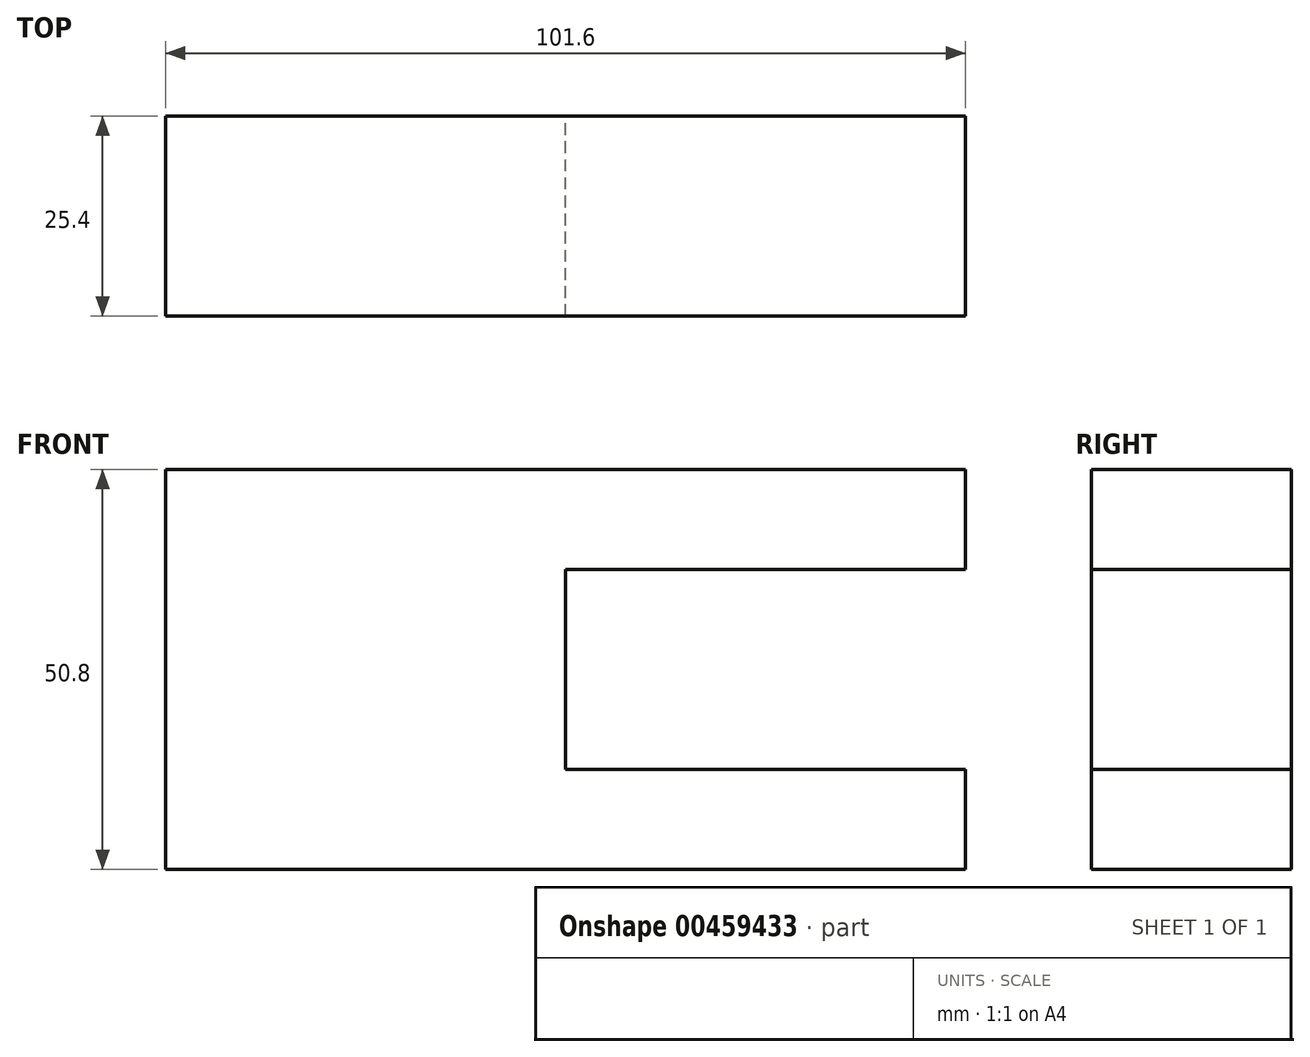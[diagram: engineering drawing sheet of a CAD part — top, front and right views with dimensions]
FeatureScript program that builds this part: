
annotation { "Feature Type Name" : "Feature", "Feature Type Description" : "" }
export const myFeature = defineFeature(function(context is Context, id is Id, definition is map)
    precondition{}
    {
        {
            var Q0;
            Q0=qCreatedBy(makeId("Front.planeOp"),FACE);
            var sketch = newSketch(context, id + "F0", { "sketchPlane" : qUnion([Q0])});
            skLineSegment(sketch, "E0.bottom", {"start": v(-50.8, 25.4) * mm, "end": v(50.8, 25.4) * mm});
            skLineSegment(sketch, "E0.top", {"start": v(-50.8, -25.4) * mm, "end": v(50.8, -25.4) * mm});
            skLineSegment(sketch, "E0.left", {"start": v(-50.8, 25.4) * mm, "end": v(-50.8, -25.4) * mm});
            skLineSegment(sketch, "E0.right", {"start": v(50.8, 25.4) * mm, "end": v(50.8, -25.4) * mm});
            skPoint(sketch, "E0.middle", {"position": v(0, 0) * mm});
            skSolve(sketch);
        }
        {
            var Q0;
            Q0=makeQuery(id+"F0.imprint","IMPRINT",FACE,{"disambiguationData":[TD([[makeQuery(id+"F0.imprint","IMPRINT",EDGE,{"derivedFrom":sQuery(id+"F0.wireOp",EDGE,"E0.bottom")}),-1.0]])]});
            extrude(context, id + "F1", {"entities" : qUnion([Q0]), "depth" : 25.4 * mm});
        }
        {
            var Q0;
            Q0=qCreatedBy(makeId("Front.planeOp"),FACE);
            var sketch = newSketch(context, id + "F2", { "sketchPlane" : qUnion([Q0])});
            skLineSegment(sketch, "E1.bottom", {"start": v(50.8, -12.7) * mm, "end": v(0, -12.7) * mm});
            skLineSegment(sketch, "E1.top", {"start": v(50.8, 12.7) * mm, "end": v(0, 12.7) * mm});
            skLineSegment(sketch, "E1.left", {"start": v(50.8, -12.7) * mm, "end": v(50.8, 12.7) * mm});
            skLineSegment(sketch, "E1.right", {"start": v(0, -12.7) * mm, "end": v(0, 12.7) * mm});
            skSolve(sketch);
        }
        {
            var Q0;
            Q0 = qSketchRegion(id + "F2", true);
            extrude(context, id + "F3", {"entities" : qUnion([Q0]), "operationType" : NewBodyOperationType.REMOVE, "endBound" : BoundingType.THROUGH_ALL, "oppositeDirection" : true, "depth" : 25.4 * mm});
        }
        {
            var Q0;
            Q0 = qSketchRegion(id + "F2", true);
            extrude(context, id + "F4", {"entities" : qUnion([Q0]), "operationType" : NewBodyOperationType.REMOVE, "endBound" : BoundingType.THROUGH_ALL, "depth" : 25.4 * mm});
        }
    });
